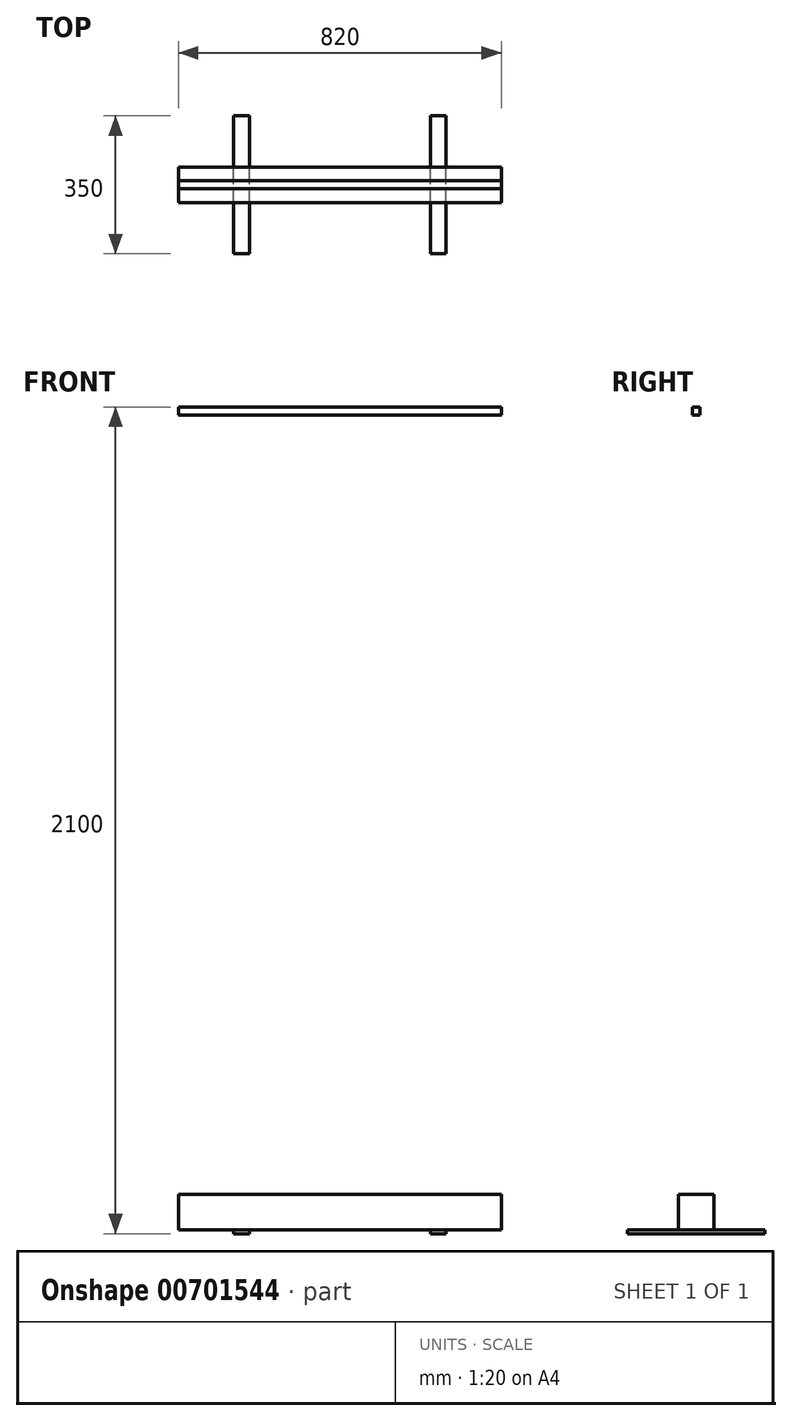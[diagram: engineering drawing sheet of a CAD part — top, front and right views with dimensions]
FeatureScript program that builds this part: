
annotation { "Feature Type Name" : "Feature", "Feature Type Description" : "" }
export const myFeature = defineFeature(function(context is Context, id is Id, definition is map)
    precondition{}
    {
        {
            var Q0;
            Q0=qCreatedBy(makeId("Right.planeOp"),FACE);
            var sketch = newSketch(context, id + "F0", { "sketchPlane" : qUnion([Q0])});
            skLineSegment(sketch, "E0.bottom", {"start": v(45, 0) * mm, "end": v(-45, 0) * mm});
            skLineSegment(sketch, "E0.top", {"start": v(45, 90) * mm, "end": v(-45, 90) * mm});
            skLineSegment(sketch, "E0.left", {"start": v(45, 0) * mm, "end": v(45, 90) * mm});
            skLineSegment(sketch, "E0.right", {"start": v(-45, 0) * mm, "end": v(-45, 90) * mm});
            skPoint(sketch, "E0.middle", {"position": v(0, 45) * mm});
            skLineSegment(sketch, "E1.bottom", {"start": v(0.5, 90) * mm, "end": v(-0.5, 90) * mm});
            skLineSegment(sketch, "E1.top", {"start": v(0.5, 2070) * mm, "end": v(-0.5, 2070) * mm});
            skLineSegment(sketch, "E1.left", {"start": v(0.5, 90) * mm, "end": v(0.5, 2070) * mm});
            skLineSegment(sketch, "E1.right", {"start": v(-0.5, 90) * mm, "end": v(-0.5, 2070) * mm});
            skPoint(sketch, "E1.middle", {"position": v(0, 1080) * mm});
            skLineSegment(sketch, "E2.bottom", {"start": v(-10, 2070) * mm, "end": v(10, 2070) * mm});
            skLineSegment(sketch, "E2.top", {"start": v(-10, 2090) * mm, "end": v(10, 2090) * mm});
            skLineSegment(sketch, "E2.left", {"start": v(-10, 2070) * mm, "end": v(-10, 2090) * mm});
            skLineSegment(sketch, "E2.right", {"start": v(10, 2070) * mm, "end": v(10, 2090) * mm});
            skPoint(sketch, "E2.middle", {"position": v(0, 2080) * mm});
            skSolve(sketch);
        }
        {
            var Q0;
            Q0=makeQuery(id+"F0.imprint","IMPRINT",FACE,{"disambiguationData":[TD([[makeQuery(id+"F0.imprint","IMPRINT",EDGE,{"derivedFrom":sQuery(id+"F0.wireOp",EDGE,"E0.bottom")}),-1.0]])]});
            var Q1;
            Q1=makeQuery(id+"F0.imprint","IMPRINT",FACE,{"disambiguationData":[TD([[makeQuery(id+"F0.imprint","IMPRINT",EDGE,{"derivedFrom":sQuery(id+"F0.wireOp",EDGE,"E1.bottom")}),-1.0]])]});
            var Q2;
            Q2=makeQuery(id+"F0.imprint","IMPRINT",FACE,{"disambiguationData":[TD([[makeQuery(id+"F0.imprint","IMPRINT",EDGE,{"derivedFrom":sQuery(id+"F0.wireOp",EDGE,"E2.top")}),-1.0]])]});
            extrude(context, id + "F1", {"entities" : qUnion([Q0, Q1, Q2]), "depth" : 410 * mm, "offsetDistance" : 25 * mm, "hasSecondDirection" : true, "secondDirectionOppositeDirection" : true, "secondDirectionDepth" : 410 * mm});
        }
        {
            var Q0;
            Q0=makeQuery(id+"F1.opExtrude","SWEPT_FACE",FACE,{"disambiguationData":[OSD([sQuery(id+"F0.wireOp",EDGE,"E0.bottom")])]});
            var sketch = newSketch(context, id + "F2", { "sketchPlane" : qUnion([Q0])});
            skLineSegment(sketch, "E3.bottom", {"start": v(-230, 175) * mm, "end": v(-270, 175) * mm});
            skLineSegment(sketch, "E3.top", {"start": v(-230, -175) * mm, "end": v(-270, -175) * mm});
            skLineSegment(sketch, "E3.left", {"start": v(-230, 175) * mm, "end": v(-230, -175) * mm});
            skLineSegment(sketch, "E3.right", {"start": v(-270, 175) * mm, "end": v(-270, -175) * mm});
            skPoint(sketch, "E3.middle", {"position": v(-250, 0) * mm});
            skLineSegment(sketch, "E4.MirrorCS", {"start": v(-190, 175) * mm, "end": v(-190, -175) * mm});
            skLineSegment(sketch, "E5.MirrorCS", {"start": v(-230, 175) * mm, "end": v(-190, 175) * mm});
            skLineSegment(sketch, "E6.MirrorCS", {"start": v(230, 175) * mm, "end": v(230, -175) * mm});
            skLineSegment(sketch, "E7.MirrorCS", {"start": v(230, -175) * mm, "end": v(270, -175) * mm});
            skLineSegment(sketch, "E8.MirrorCS", {"start": v(270, 175) * mm, "end": v(270, -175) * mm});
            skLineSegment(sketch, "E9.MirrorCS", {"start": v(230, 175) * mm, "end": v(270, 175) * mm});
            skSolve(sketch);
        }
        {
            var Q0;
            Q0 = qSketchRegion(id + "F2", true);
            extrude(context, id + "F3", {"entities" : qUnion([Q0]), "operationType" : NewBodyOperationType.ADD, "depth" : 10 * mm, "offsetDistance" : 25 * mm});
        }
    });
